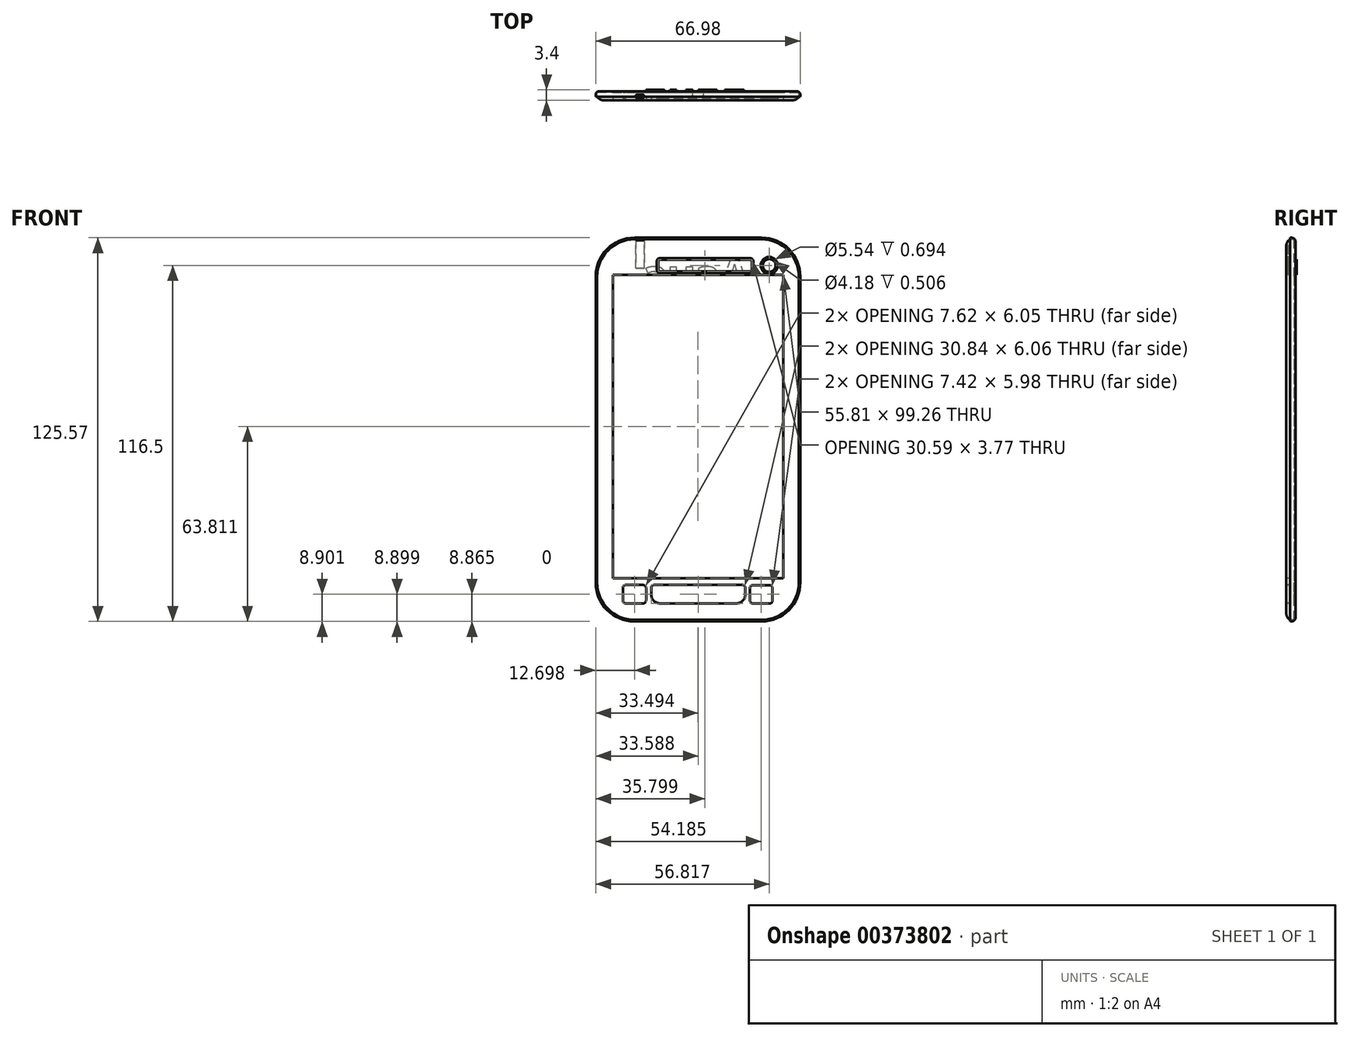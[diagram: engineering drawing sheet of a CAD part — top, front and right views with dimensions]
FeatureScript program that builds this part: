
annotation { "Feature Type Name" : "Feature", "Feature Type Description" : "" }
export const myFeature = defineFeature(function(context is Context, id is Id, definition is map)
    precondition{}
    {
        {
            var Q0;
            Q0=qCreatedBy(makeId("Front.planeOp"),FACE);
            var sketch = newSketch(context, id + "F0", { "sketchPlane" : qUnion([Q0])});
            skLineSegment(sketch, "E0.bottom", {"start": v(-16.09, 55.13) * mm, "end": v(25.5, 55.13) * mm});
            skLineSegment(sketch, "E0.top", {"start": v(-16.09, -70.44) * mm, "end": v(25.5, -70.44) * mm});
            skLineSegment(sketch, "E0.left", {"start": v(-28.79, 42.43) * mm, "end": v(-28.79, -57.74) * mm});
            skLineSegment(sketch, "E0.right", {"start": v(38.2, 42.43) * mm, "end": v(38.2, -57.74) * mm});
            skPoint(sketch, "E1.visualSharp", {"position": v(-28.79, -70.44) * mm});
            skArc(sketch, "E1.filletArc", {"start": v(-28.79, -57.74) * mm, "mid": v(-25.07, -66.72) * mm, "end": v(-16.09, -70.44) * mm});
            skPoint(sketch, "E2.visualSharp", {"position": v(38.2, -70.44) * mm});
            skArc(sketch, "E2.filletArc", {"start": v(25.5, -70.44) * mm, "mid": v(34.47, -66.72) * mm, "end": v(38.2, -57.74) * mm});
            skPoint(sketch, "E3.visualSharp", {"position": v(38.2, 55.13) * mm});
            skArc(sketch, "E3.filletArc", {"start": v(38.2, 42.43) * mm, "mid": v(34.47, 51.41) * mm, "end": v(25.5, 55.13) * mm});
            skPoint(sketch, "E4.visualSharp", {"position": v(-28.79, 55.13) * mm});
            skArc(sketch, "E4.filletArc", {"start": v(-16.09, 55.13) * mm, "mid": v(-25.07, 51.41) * mm, "end": v(-28.79, 42.43) * mm});
            skSolve(sketch);
        }
        {
            var Q0;
            Q0=makeQuery(id+"F0.imprint","IMPRINT",FACE,{"disambiguationData":[TD([[makeQuery(id+"F0.imprint","IMPRINT",EDGE,{"derivedFrom":sQuery(id+"F0.wireOp",EDGE,"E0.bottom")}),-1.0]])]});
            extrude(context, id + "F1", {"entities" : qUnion([Q0]), "depth" : 1.8 * mm});
        }
        {
            var Q0;
            Q0=makeQuery(id+"F1.opExtrude","CAP_FACE",FACE,{"disambiguationData":[OSD([sQuery(id+"F0.wireOp",EDGE,"E0.bottom"),sQuery(id+"F0.wireOp",EDGE,"E0.top"),sQuery(id+"F0.wireOp",EDGE,"E0.left"),sQuery(id+"F0.wireOp",EDGE,"E0.right"),sQuery(id+"F0.wireOp",EDGE,"E1.filletArc"),sQuery(id+"F0.wireOp",EDGE,"E2.filletArc"),sQuery(id+"F0.wireOp",EDGE,"E3.filletArc"),sQuery(id+"F0.wireOp",EDGE,"E4.filletArc")])],"isStart":false});
            shell(context, id + "F2", {"entities" : qUnion([Q0]), "thickness" : 0.5 * mm});
        }
        {
            var Q0;
            Q0=makeQuery(id+"F1.opExtrude","CAP_FACE",FACE,{"disambiguationData":[OSD([sQuery(id+"F0.wireOp",EDGE,"E0.bottom"),sQuery(id+"F0.wireOp",EDGE,"E0.top"),sQuery(id+"F0.wireOp",EDGE,"E0.left"),sQuery(id+"F0.wireOp",EDGE,"E0.right"),sQuery(id+"F0.wireOp",EDGE,"E1.filletArc"),sQuery(id+"F0.wireOp",EDGE,"E2.filletArc"),sQuery(id+"F0.wireOp",EDGE,"E3.filletArc"),sQuery(id+"F0.wireOp",EDGE,"E4.filletArc")])],"isStart":true});
            var sketch = newSketch(context, id + "F3", { "sketchPlane" : qUnion([Q0])});
            skText(sketch, "E5", { "text": "Asus \n ZEN\n    5", "fontName": "OpenSans-Bold.ttf"});
            const initialGuessF3  = {"E5": [-0.0218, 0.03744, 1, 0, 0.01072]};
            skSetInitialGuess(sketch, initialGuessF3);
            skSolve(sketch);
        }
        {
            var Q0;
            Q0 = qSketchRegion(id + "F3", true);
            extrude(context, id + "F4", {"entities" : qUnion([Q0]), "operationType" : NewBodyOperationType.ADD, "depth" : 0.4 * mm});
        }
        {
            var Q0;
            Q0=makeQuery(id+"F1.opExtrude","CAP_FACE",FACE,{"disambiguationData":[OSD([sQuery(id+"F0.wireOp",EDGE,"E0.bottom"),sQuery(id+"F0.wireOp",EDGE,"E0.top"),sQuery(id+"F0.wireOp",EDGE,"E0.left"),sQuery(id+"F0.wireOp",EDGE,"E0.right"),sQuery(id+"F0.wireOp",EDGE,"E1.filletArc"),sQuery(id+"F0.wireOp",EDGE,"E2.filletArc"),sQuery(id+"F0.wireOp",EDGE,"E3.filletArc"),sQuery(id+"F0.wireOp",EDGE,"E4.filletArc")])],"isStart":false});
            var sketch = newSketch(context, id + "F5", { "sketchPlane" : qUnion([Q0])});
            skLineSegment(sketch, "E6.bottom", {"start": v(-16.09, 55.13) * mm, "end": v(25.69, 55.13) * mm});
            skLineSegment(sketch, "E6.top", {"start": v(-16.09, -70.44) * mm, "end": v(25.69, -70.44) * mm});
            skLineSegment(sketch, "E6.left", {"start": v(-28.79, 42.43) * mm, "end": v(-28.79, -57.74) * mm});
            skLineSegment(sketch, "E6.right", {"start": v(38.39, 42.43) * mm, "end": v(38.39, -57.74) * mm});
            skPoint(sketch, "E7.visualSharp", {"position": v(-28.79, -70.44) * mm});
            skArc(sketch, "E7.filletArc", {"start": v(-28.79, -57.74) * mm, "mid": v(-25.07, -66.72) * mm, "end": v(-16.09, -70.44) * mm});
            skPoint(sketch, "E8.visualSharp", {"position": v(38.39, -70.44) * mm});
            skArc(sketch, "E8.filletArc", {"start": v(25.69, -70.44) * mm, "mid": v(34.67, -66.72) * mm, "end": v(38.39, -57.74) * mm});
            skPoint(sketch, "E9.visualSharp", {"position": v(38.39, 55.13) * mm});
            skArc(sketch, "E9.filletArc", {"start": v(38.39, 42.43) * mm, "mid": v(34.67, 51.41) * mm, "end": v(25.69, 55.13) * mm});
            skPoint(sketch, "E10.visualSharp", {"position": v(-28.79, 55.13) * mm});
            skArc(sketch, "E10.filletArc", {"start": v(-16.09, 55.13) * mm, "mid": v(-25.07, 51.41) * mm, "end": v(-28.79, 42.43) * mm});
            skSolve(sketch);
        }
        {
            var Q0;
            {var subQ3=sQuery(id+"F0.wireOp",EDGE,"E0.bottom");Q0=makeQuery(id+"F5.imprint","IMPRINT",FACE,{"disambiguationData":[TD([[makeQuery(id+"F5.imprint","IMPRINT",EDGE,{"derivedFrom":makeQuery(id+"F2.opShell","OFFSET_EDGE",EDGE,{"disambiguationData":[OSD([subQ3]),TDD([makeQuery(id+"F1.opExtrude","CAP_EDGE",EDGE,{"disambiguationData":[OSD([subQ3])],"isStart":false})])]})}),-1.0]])]});}
            extrude(context, id + "F6", {"entities" : qUnion([Q0]), "depth" : 1.2 * mm});
        }
        {
            var Q0;
            Q0=makeQuery(id+"F6.opExtrude","CAP_EDGE",EDGE,{"disambiguationData":[OSD([sQuery(id+"F0.wireOp",EDGE,"E2.filletArc")])],"isStart":false});
            var Q1;
            Q1=makeQuery(id+"F6.opExtrude","CAP_EDGE",EDGE,{"disambiguationData":[OSD([sQuery(id+"F0.wireOp",EDGE,"E0.right")])],"isStart":false});
            fillet(context, id + "F7", {"entities" : qUnion([Q0, Q1]), "radius" : 2.5 * mm, "tangentPropagation" : true, "allowEdgeOverflow" : false});
        }
        {
            var Q0;
            Q0=makeQuery(id+"F1.opExtrude","CAP_EDGE",EDGE,{"disambiguationData":[OSD([sQuery(id+"F0.wireOp",EDGE,"E1.filletArc")])],"isStart":true});
            var Q1;
            Q1=makeQuery(id+"F1.opExtrude","CAP_EDGE",EDGE,{"disambiguationData":[OSD([sQuery(id+"F0.wireOp",EDGE,"E0.top")])],"isStart":true});
            var Q2;
            Q2=makeQuery(id+"F1.opExtrude","CAP_EDGE",EDGE,{"disambiguationData":[OSD([sQuery(id+"F0.wireOp",EDGE,"E2.filletArc")])],"isStart":true});
            var Q3;
            Q3=makeQuery(id+"F1.opExtrude","CAP_EDGE",EDGE,{"disambiguationData":[OSD([sQuery(id+"F0.wireOp",EDGE,"E0.right")])],"isStart":true});
            var Q4;
            Q4=makeQuery(id+"F1.opExtrude","CAP_EDGE",EDGE,{"disambiguationData":[OSD([sQuery(id+"F0.wireOp",EDGE,"E0.left")])],"isStart":true});
            var Q5;
            Q5=makeQuery(id+"F1.opExtrude","CAP_EDGE",EDGE,{"disambiguationData":[OSD([sQuery(id+"F0.wireOp",EDGE,"E4.filletArc")])],"isStart":true});
            var Q6;
            Q6=makeQuery(id+"F1.opExtrude","CAP_EDGE",EDGE,{"disambiguationData":[OSD([sQuery(id+"F0.wireOp",EDGE,"E0.bottom")])],"isStart":true});
            var Q7;
            Q7=makeQuery(id+"F1.opExtrude","CAP_EDGE",EDGE,{"disambiguationData":[OSD([sQuery(id+"F0.wireOp",EDGE,"E3.filletArc")])],"isStart":true});
            fillet(context, id + "F8", {"entities" : qUnion([Q0, Q1, Q2, Q3, Q4, Q5, Q6, Q7]), "radius" : 1.2 * mm, "tangentPropagation" : true, "allowEdgeOverflow" : false});
        }
        {
            var Q0;
            Q0=makeQuery(id+"F6.opExtrude","CAP_FACE",FACE,{"disambiguationData":[OSD([sQuery(id+"F0.wireOp",EDGE,"E0.bottom"),sQuery(id+"F0.wireOp",EDGE,"E0.top"),sQuery(id+"F0.wireOp",EDGE,"E0.left"),sQuery(id+"F0.wireOp",EDGE,"E0.right"),sQuery(id+"F0.wireOp",EDGE,"E1.filletArc"),sQuery(id+"F0.wireOp",EDGE,"E2.filletArc"),sQuery(id+"F0.wireOp",EDGE,"E3.filletArc"),sQuery(id+"F0.wireOp",EDGE,"E4.filletArc")])],"isStart":false});
            var sketch = newSketch(context, id + "F9", { "sketchPlane" : qUnion([Q0])});
            skLineSegment(sketch, "E11.bottom", {"start": v(-18.2, 49.55) * mm, "end": v(27.61, 49.55) * mm});
            skLineSegment(sketch, "E11.top", {"start": v(-17.2, -64.86) * mm, "end": v(26.61, -64.86) * mm});
            skLineSegment(sketch, "E11.left", {"start": v(-23.2, 44.55) * mm, "end": v(-23.2, -58.86) * mm});
            skLineSegment(sketch, "E11.right", {"start": v(32.61, 44.55) * mm, "end": v(32.61, -58.86) * mm});
            skPoint(sketch, "E12.visualSharp", {"position": v(-23.2, 49.55) * mm});
            skArc(sketch, "E12.filletArc", {"start": v(-18.2, 49.55) * mm, "mid": v(-21.74, 48.08) * mm, "end": v(-23.2, 44.55) * mm});
            skPoint(sketch, "E13.visualSharp", {"position": v(32.61, 49.55) * mm});
            skArc(sketch, "E13.filletArc", {"start": v(32.61, 44.55) * mm, "mid": v(31.15, 48.08) * mm, "end": v(27.61, 49.55) * mm});
            skPoint(sketch, "E14.visualSharp", {"position": v(-23.2, -64.86) * mm});
            skArc(sketch, "E14.filletArc", {"start": v(-23.2, -58.86) * mm, "mid": v(-21.44, -63.1) * mm, "end": v(-17.2, -64.86) * mm});
            skPoint(sketch, "E15.visualSharp", {"position": v(32.61, -64.86) * mm});
            skArc(sketch, "E15.filletArc", {"start": v(26.61, -64.86) * mm, "mid": v(30.85, -63.1) * mm, "end": v(32.61, -58.86) * mm});
            skSolve(sketch);
        }
        {
            var Q0;
            Q0=makeQuery(id+"F9.imprint","IMPRINT",FACE,{"disambiguationData":[TD([[makeQuery(id+"F9.imprint","IMPRINT",EDGE,{"derivedFrom":sQuery(id+"F9.wireOp",EDGE,"E11.bottom")}),-1.0]])]});
            var sketch = newSketch(context, id + "F10", { "sketchPlane" : qUnion([Q0])});
            skLineSegment(sketch, "E16.bottom", {"start": v(-24.05, 43) * mm, "end": v(32.88, 43) * mm});
            skLineSegment(sketch, "E16.top", {"start": v(-24.05, -56.26) * mm, "end": v(32.88, -56.26) * mm});
            skLineSegment(sketch, "E16.left", {"start": v(-24.05, 43) * mm, "end": v(-24.05, -56.26) * mm});
            skLineSegment(sketch, "E16.right", {"start": v(32.88, 43) * mm, "end": v(32.88, -56.26) * mm});
            skSolve(sketch);
        }
        {
            var Q0;
            {var subQ0=sQuery(id+"F10.wireOp",EDGE,"E16.bottom");var subQ1=makeQuery(id+"F9.imprint","IMPRINT",EDGE,{"derivedFrom":sQuery(id+"F9.wireOp",EDGE,"E11.left")});var subQ2=makeQuery(id+"F10.imprint","INTERSECT",VERTEX,{"derivedFrom":[subQ1,subQ0]});Q0=makeQuery(id+"F10.imprint","IMPRINT",FACE,{"disambiguationData":[TD([[makeQuery(id+"F10.imprint","IMPRINT",EDGE,{"disambiguationData":[TD([[subQ2,-1.0]])],"derivedFrom":subQ0}),-1.0]])]});}
            extrude(context, id + "F11", {"entities" : qUnion([Q0]), "operationType" : NewBodyOperationType.REMOVE, "oppositeDirection" : true, "depth" : 5 * mm});
        }
        {
            var Q0;
            Q0=makeQuery(id+"F10.imprint","IMPRINT",FACE,{"disambiguationData":[TD([[makeQuery(id+"F10.imprint","IMPRINT",EDGE,{"derivedFrom":makeQuery(id+"F9.imprint","IMPRINT",EDGE,{"derivedFrom":sQuery(id+"F9.wireOp",EDGE,"E11.top")})}),1.0]])]});
            var sketch = newSketch(context, id + "F12", { "sketchPlane" : qUnion([Q0])});
            skLineSegment(sketch, "E17.bottom", {"start": v(19.22, -58.51) * mm, "end": v(-9.62, -58.51) * mm});
            skLineSegment(sketch, "E17.top", {"start": v(17.22, -64.57) * mm, "end": v(-7.62, -64.57) * mm});
            skLineSegment(sketch, "E17.left", {"start": v(20.22, -59.51) * mm, "end": v(20.22, -61.57) * mm});
            skLineSegment(sketch, "E17.right", {"start": v(-10.62, -59.51) * mm, "end": v(-10.62, -61.57) * mm});
            skPoint(sketch, "E18.visualSharp", {"position": v(-10.62, -64.57) * mm});
            skArc(sketch, "E18.filletArc", {"start": v(-10.62, -61.57) * mm, "mid": v(-9.75, -63.7) * mm, "end": v(-7.62, -64.57) * mm});
            skPoint(sketch, "E19.visualSharp", {"position": v(20.22, -64.57) * mm});
            skArc(sketch, "E19.filletArc", {"start": v(17.22, -64.57) * mm, "mid": v(19.34, -63.7) * mm, "end": v(20.22, -61.57) * mm});
            skPoint(sketch, "E20.startSnap0", {"position": v(4.8, -58.51) * mm});
            skPoint(sketch, "E20.endSnap0", {"position": v(4.8, -58.51) * mm});
            skLineSegment(sketch, "E21.bottom", {"start": v(-13.28, -58.51) * mm, "end": v(-18.9, -58.51) * mm});
            skLineSegment(sketch, "E21.top", {"start": v(-13.33, -64.57) * mm, "end": v(-18.9, -64.57) * mm});
            skLineSegment(sketch, "E21.left", {"start": v(-12.28, -59.51) * mm, "end": v(-12.28, -63.51) * mm});
            skLineSegment(sketch, "E21.right", {"start": v(-19.9, -59.51) * mm, "end": v(-19.9, -63.57) * mm});
            skLineSegment(sketch, "E22.MirrorCS", {"start": v(29.1, -59.59) * mm, "end": v(29.1, -63.57) * mm});
            skLineSegment(sketch, "E23.MirrorCS", {"start": v(22.68, -64.57) * mm, "end": v(28.1, -64.57) * mm});
            skLineSegment(sketch, "E24.MirrorCS", {"start": v(21.68, -59.59) * mm, "end": v(21.68, -63.57) * mm});
            skLineSegment(sketch, "E25.MirrorCS", {"start": v(22.68, -58.59) * mm, "end": v(28.1, -58.59) * mm});
            skPoint(sketch, "E26.visualSharp", {"position": v(21.68, -58.59) * mm});
            skArc(sketch, "E26.filletArc", {"start": v(22.68, -58.59) * mm, "mid": v(21.98, -58.88) * mm, "end": v(21.68, -59.59) * mm});
            skArc(sketch, "E27.filletArc", {"start": v(29.1, -59.59) * mm, "mid": v(28.81, -58.88) * mm, "end": v(28.1, -58.59) * mm});
            skPoint(sketch, "E28.visualSharp", {"position": v(-12.28, -58.51) * mm});
            skArc(sketch, "E28.filletArc", {"start": v(-12.28, -59.51) * mm, "mid": v(-12.57, -58.8) * mm, "end": v(-13.28, -58.51) * mm});
            skPoint(sketch, "E29.visualSharp", {"position": v(-19.9, -58.51) * mm});
            skArc(sketch, "E29.filletArc", {"start": v(-18.9, -58.51) * mm, "mid": v(-19.6, -58.8) * mm, "end": v(-19.9, -59.51) * mm});
            skPoint(sketch, "E30.visualSharp", {"position": v(-19.9, -64.57) * mm});
            skArc(sketch, "E30.filletArc", {"start": v(-19.9, -63.57) * mm, "mid": v(-19.6, -64.27) * mm, "end": v(-18.9, -64.57) * mm});
            skPoint(sketch, "E31.visualSharp", {"position": v(-12.28, -64.57) * mm});
            skArc(sketch, "E31.filletArc", {"start": v(-13.28, -64.57) * mm, "mid": v(-12.57, -64.27) * mm, "end": v(-12.28, -63.57) * mm});
            skPoint(sketch, "E32.visualSharp", {"position": v(-10.62, -58.51) * mm});
            skArc(sketch, "E32.filletArc", {"start": v(-9.62, -58.51) * mm, "mid": v(-10.33, -58.8) * mm, "end": v(-10.62, -59.51) * mm});
            skPoint(sketch, "E33.visualSharp", {"position": v(20.22, -58.51) * mm});
            skArc(sketch, "E33.filletArc", {"start": v(20.22, -59.51) * mm, "mid": v(19.93, -58.8) * mm, "end": v(19.22, -58.51) * mm});
            skPoint(sketch, "E34.visualSharp", {"position": v(21.68, -64.57) * mm});
            skArc(sketch, "E34.filletArc", {"start": v(21.68, -63.57) * mm, "mid": v(21.98, -64.27) * mm, "end": v(22.68, -64.57) * mm});
            skArc(sketch, "E35.filletArc", {"start": v(28.1, -64.57) * mm, "mid": v(28.81, -64.27) * mm, "end": v(29.1, -63.57) * mm});
            skArc(sketch, "E36.filletArc", {"start": v(-13.33, -64.57) * mm, "mid": v(-12.59, -64.26) * mm, "end": v(-12.28, -63.51) * mm});
            skSolve(sketch);
        }
        {
            var Q0;
            Q0=makeQuery(id+"F12.imprint","IMPRINT",FACE,{"disambiguationData":[TD([[makeQuery(id+"F12.imprint","IMPRINT",EDGE,{"derivedFrom":sQuery(id+"F12.wireOp",EDGE,"E21.bottom")}),1.0]])]});
            var Q1;
            Q1=makeQuery(id+"F12.imprint","IMPRINT",FACE,{"disambiguationData":[TD([[makeQuery(id+"F12.imprint","IMPRINT",EDGE,{"derivedFrom":sQuery(id+"F12.wireOp",EDGE,"E22.MirrorCS")}),-1.0]])]});
            var Q2;
            Q2=makeQuery(id+"F12.imprint","IMPRINT",FACE,{"disambiguationData":[TD([[makeQuery(id+"F12.imprint","IMPRINT",EDGE,{"derivedFrom":sQuery(id+"F12.wireOp",EDGE,"E17.bottom")}),1.0]])]});
            extrude(context, id + "F13", {"entities" : qUnion([Q0, Q1, Q2]), "operationType" : NewBodyOperationType.REMOVE, "oppositeDirection" : true, "depth" : 25 * mm});
        }
        {
            var Q0;
            Q0=makeQuery(id+"F10.imprint","IMPRINT",FACE,{"disambiguationData":[TD([[makeQuery(id+"F10.imprint","IMPRINT",EDGE,{"derivedFrom":makeQuery(id+"F9.imprint","IMPRINT",EDGE,{"derivedFrom":sQuery(id+"F9.wireOp",EDGE,"E11.bottom")})}),-1.0]])]});
            var sketch = newSketch(context, id + "F14", { "sketchPlane" : qUnion([Q0])});
            skLineSegment(sketch, "E37.bottom", {"start": v(-7.78, 48.44) * mm, "end": v(21.8, 48.44) * mm});
            skLineSegment(sketch, "E37.top", {"start": v(-7.78, 43.68) * mm, "end": v(21.8, 43.68) * mm});
            skLineSegment(sketch, "E37.left", {"start": v(-8.78, 47.44) * mm, "end": v(-8.78, 44.68) * mm});
            skLineSegment(sketch, "E37.right", {"start": v(22.8, 47.44) * mm, "end": v(22.8, 44.68) * mm});
            skCircle(sketch, "E38", {"center": v(28.03, 46.06) * mm, "radius": 2.77 * mm});
            skPoint(sketch, "E38.centerSnap0", {"position": v(22.8, 46.06) * mm});
            skCircle(sketch, "E39", {"center": v(28.03, 46.06) * mm, "radius": 2.1 * mm});
            skPoint(sketch, "E40.visualSharp", {"position": v(22.8, 48.44) * mm});
            skArc(sketch, "E40.filletArc", {"start": v(22.8, 47.44) * mm, "mid": v(22.5, 48.15) * mm, "end": v(21.8, 48.44) * mm});
            skPoint(sketch, "E41.visualSharp", {"position": v(22.8, 43.68) * mm});
            skArc(sketch, "E41.filletArc", {"start": v(21.8, 43.68) * mm, "mid": v(22.5, 43.97) * mm, "end": v(22.8, 44.68) * mm});
            skPoint(sketch, "E42.visualSharp", {"position": v(-8.78, 48.44) * mm});
            skArc(sketch, "E42.filletArc", {"start": v(-7.78, 48.44) * mm, "mid": v(-8.5, 48.15) * mm, "end": v(-8.78, 47.44) * mm});
            skPoint(sketch, "E43.visualSharp", {"position": v(-8.78, 43.68) * mm});
            skArc(sketch, "E43.filletArc", {"start": v(-8.78, 44.68) * mm, "mid": v(-8.5, 43.97) * mm, "end": v(-7.78, 43.68) * mm});
            skLineSegment(sketch, "E44.0", {"start": v(-7.78, 44.18) * mm, "end": v(21.8, 44.18) * mm});
            skArc(sketch, "E44.1", {"start": v(-8.28, 44.68) * mm, "mid": v(-8.14, 44.32) * mm, "end": v(-7.78, 44.18) * mm});
            skArc(sketch, "E44.2", {"start": v(21.8, 44.18) * mm, "mid": v(22.15, 44.32) * mm, "end": v(22.3, 44.68) * mm});
            skLineSegment(sketch, "E44.3", {"start": v(-8.28, 47.44) * mm, "end": v(-8.28, 44.68) * mm});
            skLineSegment(sketch, "E44.4", {"start": v(22.3, 47.44) * mm, "end": v(22.3, 44.68) * mm});
            skArc(sketch, "E44.5", {"start": v(22.3, 47.44) * mm, "mid": v(22.15, 47.8) * mm, "end": v(21.8, 47.94) * mm});
            skLineSegment(sketch, "E44.6", {"start": v(-7.78, 47.94) * mm, "end": v(21.8, 47.94) * mm});
            skArc(sketch, "E44.7", {"start": v(-7.78, 47.94) * mm, "mid": v(-8.14, 47.8) * mm, "end": v(-8.28, 47.44) * mm});
            skSolve(sketch);
        }
        {
            var Q0;
            Q0=makeQuery(id+"F14.imprint","IMPRINT",FACE,{"disambiguationData":[TD([[makeQuery(id+"F14.imprint","IMPRINT",EDGE,{"derivedFrom":sQuery(id+"F14.wireOp",EDGE,"E44.0")}),1.0]])]});
            var Q1;
            Q1=makeQuery(id+"F14.imprint","IMPRINT",FACE,{"disambiguationData":[TD([[makeQuery(id+"F14.imprint","IMPRINT",EDGE,{"derivedFrom":sQuery(id+"F14.wireOp",EDGE,"E37.bottom")}),-1.0]])]});
            var Q2;
            Q2=makeQuery(id+"F14.imprint","IMPRINT",FACE,{"disambiguationData":[TD([[makeQuery(id+"F14.imprint","IMPRINT",EDGE,{"derivedFrom":sQuery(id+"F14.wireOp",EDGE,"E39")}),1.0]])]});
            var Q3;
            Q3=makeQuery(id+"F14.imprint","IMPRINT",FACE,{"disambiguationData":[TD([[makeQuery(id+"F14.imprint","IMPRINT",EDGE,{"derivedFrom":sQuery(id+"F14.wireOp",EDGE,"E38")}),1.0]])]});
            extrude(context, id + "F15", {"entities" : qUnion([Q0, Q1, Q2, Q3]), "operationType" : NewBodyOperationType.REMOVE, "oppositeDirection" : true, "depth" : 0.7 * mm});
        }
        {
            var Q0;
            Q0=makeQuery(id+"F14.imprint","IMPRINT",FACE,{"disambiguationData":[TD([[makeQuery(id+"F14.imprint","IMPRINT",EDGE,{"derivedFrom":sQuery(id+"F14.wireOp",EDGE,"E44.0")}),1.0]])]});
            var Q1;
            Q1=makeQuery(id+"F14.imprint","IMPRINT",FACE,{"disambiguationData":[TD([[makeQuery(id+"F14.imprint","IMPRINT",EDGE,{"derivedFrom":sQuery(id+"F14.wireOp",EDGE,"E39")}),1.0]])]});
            extrude(context, id + "F16", {"entities" : qUnion([Q0, Q1]), "oppositeDirection" : true, "depth" : 3 * mm});
        }
        {
            var Q0;
            Q0=makeQuery(id+"F16.opExtrude","SWEPT_BODY",BODY,{"disambiguationData":[OSD([sQuery(id+"F14.wireOp",EDGE,"E44.0"),sQuery(id+"F14.wireOp",EDGE,"E44.1"),sQuery(id+"F14.wireOp",EDGE,"E44.2"),sQuery(id+"F14.wireOp",EDGE,"E44.3"),sQuery(id+"F14.wireOp",EDGE,"E44.4"),sQuery(id+"F14.wireOp",EDGE,"E44.5"),sQuery(id+"F14.wireOp",EDGE,"E44.6"),sQuery(id+"F14.wireOp",EDGE,"E44.7")])]});
            var Q1;
            Q1=makeQuery(id+"F16.opExtrude","SWEPT_BODY",BODY,{"disambiguationData":[OSD([sQuery(id+"F14.wireOp",EDGE,"E39")])]});
            var Q2;
            Q2=makeQuery(id+"F6.opExtrude","SWEPT_BODY",BODY,{"disambiguationData":[OSD([sQuery(id+"F0.wireOp",EDGE,"E0.bottom"),sQuery(id+"F0.wireOp",EDGE,"E0.top"),sQuery(id+"F0.wireOp",EDGE,"E0.left"),sQuery(id+"F0.wireOp",EDGE,"E0.right"),sQuery(id+"F0.wireOp",EDGE,"E1.filletArc"),sQuery(id+"F0.wireOp",EDGE,"E2.filletArc"),sQuery(id+"F0.wireOp",EDGE,"E3.filletArc"),sQuery(id+"F0.wireOp",EDGE,"E4.filletArc")])]});
            booleanBodies(context, id + "F17", {"operationType" : BooleanOperationType.SUBTRACTION, "tools" : qUnion([Q0, Q1]), "targets" : qUnion([Q2])});
        }
        {
            var Q0;
            Q0=makeQuery(id+"F1.opExtrude","SWEPT_FACE",FACE,{"disambiguationData":[OSD([sQuery(id+"F0.wireOp",EDGE,"E0.top")])]});
            var sketch = newSketch(context, id + "F18", { "sketchPlane" : qUnion([Q0])});
            skLineSegment(sketch, "E45", {"start": v(4.7, 5.08) * mm, "end": v(4.7, -1.75) * mm, "construction": true});
            skPoint(sketch, "E45.startSnap0", {"position": v(4.7, 1.8) * mm});
            skLineSegment(sketch, "E46", {"start": v(4.7, 1.67) * mm, "end": v(2.9, 1.67) * mm});
            skLineSegment(sketch, "E47", {"start": v(2.9, 1.67) * mm, "end": v(2.9, 0.83) * mm});
            skLineSegment(sketch, "E48", {"start": v(3.2, 0.53) * mm, "end": v(4.7, 0.53) * mm});
            skLineSegment(sketch, "E49.MirrorCS", {"start": v(4.7, 1.67) * mm, "end": v(6.5, 1.67) * mm});
            skLineSegment(sketch, "E50.MirrorCS", {"start": v(6.5, 1.67) * mm, "end": v(6.5, 0.83) * mm});
            skLineSegment(sketch, "E51.MirrorCS", {"start": v(6.2, 0.53) * mm, "end": v(4.7, 0.53) * mm});
            skPoint(sketch, "E52.visualSharp", {"position": v(2.9, 0.53) * mm});
            skArc(sketch, "E52.filletArc", {"start": v(2.9, 0.83) * mm, "mid": v(2.99, 0.62) * mm, "end": v(3.2, 0.53) * mm});
            skPoint(sketch, "E53.visualSharp", {"position": v(6.5, 0.53) * mm});
            skArc(sketch, "E53.filletArc", {"start": v(6.2, 0.53) * mm, "mid": v(6.42, 0.62) * mm, "end": v(6.5, 0.83) * mm});
            skSolve(sketch);
        }
        {
            var Q0;
            Q0=makeQuery(id+"F18.imprint","IMPRINT",FACE,{"disambiguationData":[TD([[makeQuery(id+"F18.imprint","IMPRINT",EDGE,{"derivedFrom":sQuery(id+"F18.wireOp",EDGE,"E48")}),1.0]])]});
            var Q1;
            {var subQ7=sQuery(id+"F18.wireOp",EDGE,"E46");Q1=makeQuery(id+"F18.imprint","IMPRINT",FACE,{"disambiguationData":[TD([[makeQuery(id+"F18.imprint","IMPRINT",EDGE,{"derivedFrom":subQ7}),1.0]])]});}
            extrude(context, id + "F19", {"entities" : qUnion([Q0, Q1]), "operationType" : NewBodyOperationType.REMOVE, "oppositeDirection" : true, "depth" : 25 * mm});
        }
        {
            var Q0;
            {var subQ0=sQuery(id+"F0.wireOp",EDGE,"E0.left");var subQ1=sQuery(id+"F0.wireOp",EDGE,"E0.top");var subQ2=sQuery(id+"F0.wireOp",EDGE,"E0.right");var subQ3=sQuery(id+"F0.wireOp",EDGE,"E1.filletArc");var subQ4=sQuery(id+"F0.wireOp",EDGE,"E0.bottom");var subQ5=sQuery(id+"F0.wireOp",EDGE,"E2.filletArc");var subQ6=sQuery(id+"F0.wireOp",EDGE,"E3.filletArc");var subQ7=sQuery(id+"F0.wireOp",EDGE,"E4.filletArc");Q0=makeQuery(id+"F4.boolean.opBoolean","SPLIT",FACE,{"disambiguationData":[TD([makeQuery(id+"F1.opExtrude","SWEPT_FACE",FACE,{"disambiguationData":[OSD([subQ4])]})])],"derivedFrom":makeQuery(id+"F1.opExtrude","CAP_FACE",FACE,{"disambiguationData":[OSD([subQ4,subQ1,subQ0,subQ2,subQ3,subQ5,subQ6,subQ7])],"isStart":true})});}
            var sketch = newSketch(context, id + "F20", { "sketchPlane" : qUnion([Q0])});
            skCircle(sketch, "E54", {"center": v(-4.7, 33.1) * mm, "radius": 4.23 * mm});
            skSolve(sketch);
        }
        {
            var Q0;
            Q0=makeQuery(id+"F20.imprint","IMPRINT",FACE,{"disambiguationData":[TD([[makeQuery(id+"F20.imprint","IMPRINT",EDGE,{"derivedFrom":sQuery(id+"F20.wireOp",EDGE,"E54")}),1.0]])]});
            extrude(context, id + "F21", {"entities" : qUnion([Q0]), "operationType" : NewBodyOperationType.REMOVE, "oppositeDirection" : true, "depth" : 25 * mm});
        }
        {
            var Q0;
            Q0=makeQuery(id+"F1.opExtrude","SWEPT_FACE",FACE,{"disambiguationData":[OSD([sQuery(id+"F0.wireOp",EDGE,"E0.bottom")])]});
            var sketch = newSketch(context, id + "F22", { "sketchPlane" : qUnion([Q0])});
            skLineSegment(sketch, "E55.bottom", {"start": v(-15.26, -1.2) * mm, "end": v(-13.3, -1.2) * mm});
            skLineSegment(sketch, "E55.top", {"start": v(-15.26, -2.24) * mm, "end": v(-13.3, -2.24) * mm});
            skLineSegment(sketch, "E55.left", {"start": v(-15.66, -1.6) * mm, "end": v(-15.66, -1.84) * mm});
            skLineSegment(sketch, "E55.right", {"start": v(-12.9, -1.6) * mm, "end": v(-12.9, -1.84) * mm});
            skPoint(sketch, "E56.visualSharp", {"position": v(-15.66, -1.2) * mm});
            skArc(sketch, "E56.filletArc", {"start": v(-15.26, -1.2) * mm, "mid": v(-15.54, -1.32) * mm, "end": v(-15.66, -1.6) * mm});
            skPoint(sketch, "E57.visualSharp", {"position": v(-12.9, -1.2) * mm});
            skArc(sketch, "E57.filletArc", {"start": v(-12.9, -1.6) * mm, "mid": v(-13.02, -1.32) * mm, "end": v(-13.3, -1.2) * mm});
            skPoint(sketch, "E58.visualSharp", {"position": v(-15.66, -2.24) * mm});
            skArc(sketch, "E58.filletArc", {"start": v(-15.66, -1.84) * mm, "mid": v(-15.54, -2.12) * mm, "end": v(-15.26, -2.24) * mm});
            skPoint(sketch, "E59.visualSharp", {"position": v(-12.9, -2.24) * mm});
            skArc(sketch, "E59.filletArc", {"start": v(-13.3, -2.24) * mm, "mid": v(-13.02, -2.12) * mm, "end": v(-12.9, -1.84) * mm});
            skSolve(sketch);
        }
        {
            var Q0;
            Q0=makeQuery(id+"F22.imprint","IMPRINT",FACE,{"disambiguationData":[TD([[makeQuery(id+"F22.imprint","IMPRINT",EDGE,{"derivedFrom":sQuery(id+"F22.wireOp",EDGE,"E55.bottom")}),1.0]])]});
            var Q1;
            Q1=makeQuery(id+"F22.imprint","IMPRINT",FACE,{"disambiguationData":[TD([[makeQuery(id+"F22.imprint","IMPRINT",EDGE,{"derivedFrom":sQuery(id+"F22.wireOp",EDGE,"E55.top")}),1.0]])]});
            extrude(context, id + "F23", {"entities" : qUnion([Q0, Q1]), "operationType" : NewBodyOperationType.REMOVE, "oppositeDirection" : true, "depth" : 10 * mm, "hasSecondDirection" : true, "secondDirectionOppositeDirection" : false, "secondDirectionDepth" : 25 * mm});
        }
    });
